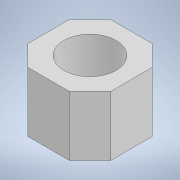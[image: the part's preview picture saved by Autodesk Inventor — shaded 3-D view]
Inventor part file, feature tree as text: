
AUTODESK INVENTOR PART (.ipt)
format: ipt  version: 2020 (Build 240168000, 168)  size: 107,008 bytes
history: native  units: in
note: dims shown in document units (in); Inventor stores cm internally (conversion verified against a paired STEP export)
features: extrude x2, sketch x2
ambient origin geometry x8: Origin, YZ Plane, XZ Plane, XY Plane, X Axis, Y Axis, Z Axis, Center Point
bodies: Solid1 (feature_tree)
feature tree (4):
  extrude  "Extrusion1"  Depth=1.3287in
  extrude  "Extrusion2"  Depth=0.9606in TaperAngle=0.0deg
  sketch  "Sketch1"  dims[d0=1.3287in d1=1.3287in]
  sketch  "Sketch2"  dims[d2=0.8362in d3=0.9606in d4=0.0in d5=0.1575in d6=0.0in]
